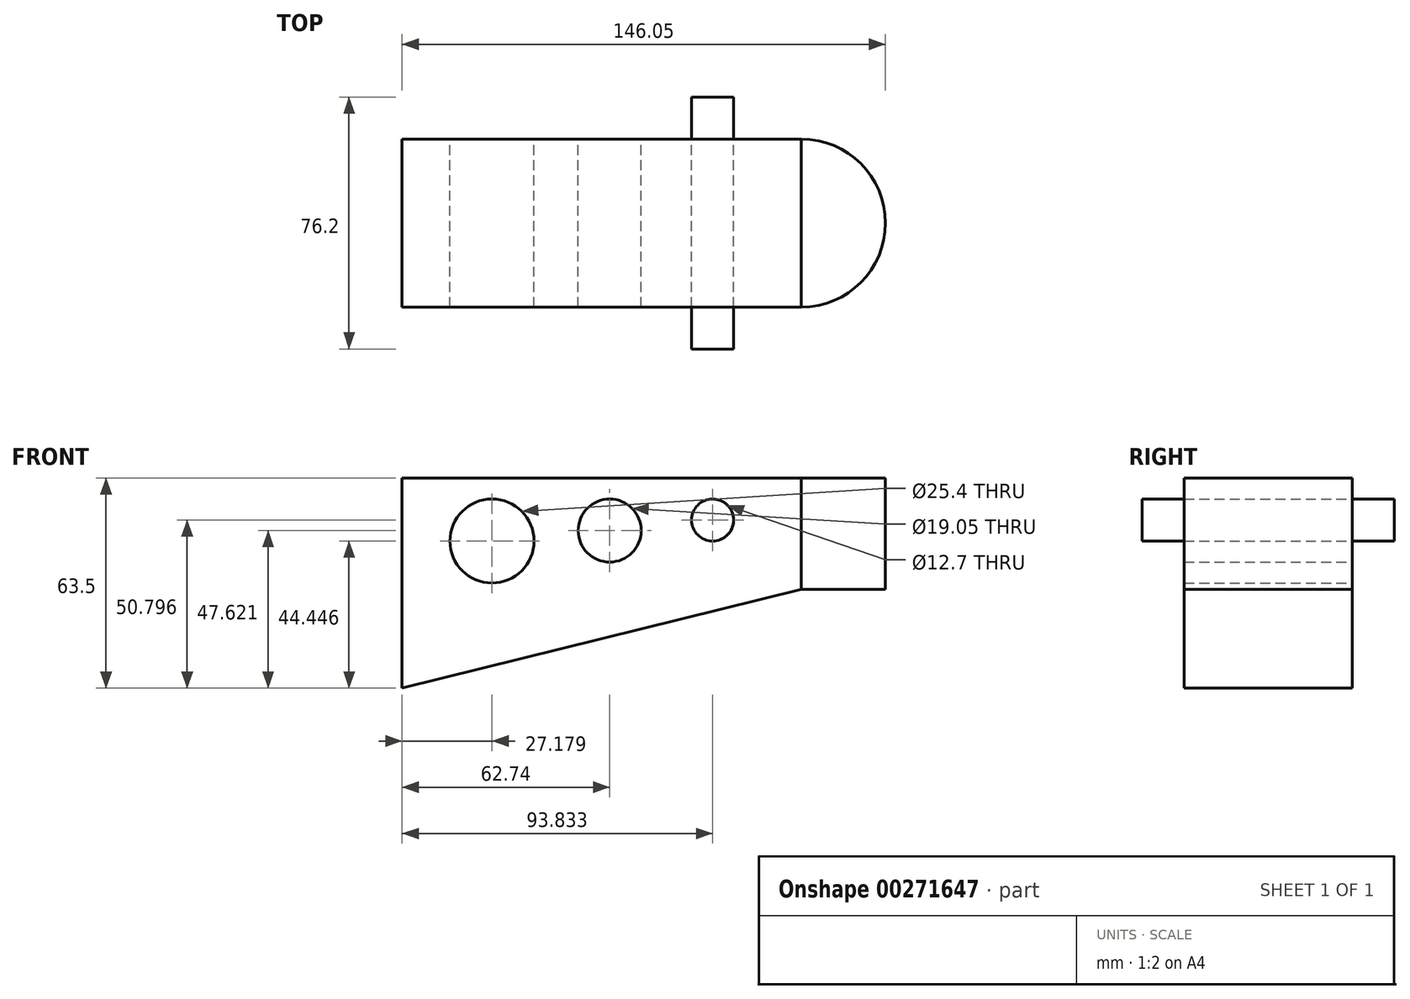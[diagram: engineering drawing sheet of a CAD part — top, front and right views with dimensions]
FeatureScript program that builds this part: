
annotation { "Feature Type Name" : "Feature", "Feature Type Description" : "" }
export const myFeature = defineFeature(function(context is Context, id is Id, definition is map)
    precondition{}
    {
        {
            var Q0;
            Q0=qCreatedBy(makeId("Front.planeOp"),FACE);
            var sketch = newSketch(context, id + "F0", { "sketchPlane" : qUnion([Q0])});
            skLineSegment(sketch, "E0", {"start": v(-62.74, 45.63) * mm, "end": v(-62.74, -17.87) * mm});
            skLineSegment(sketch, "E1", {"start": v(-62.74, -17.87) * mm, "end": v(57.9, 11.92) * mm});
            skLineSegment(sketch, "E2", {"start": v(57.9, 11.92) * mm, "end": v(57.9, 45.63) * mm});
            skLineSegment(sketch, "E3", {"start": v(57.9, 45.63) * mm, "end": v(-62.74, 45.63) * mm});
            skLineSegment(sketch, "E4.bottom", {"start": v(57.9, 45.63) * mm, "end": v(83.3, 45.63) * mm});
            skLineSegment(sketch, "E4.top", {"start": v(57.9, 11.92) * mm, "end": v(83.3, 11.92) * mm});
            skLineSegment(sketch, "E4.left", {"start": v(57.9, 45.63) * mm, "end": v(57.9, 11.92) * mm});
            skLineSegment(sketch, "E4.right", {"start": v(83.3, 45.63) * mm, "end": v(83.3, 11.92) * mm});
            skCircle(sketch, "E5", {"center": v(-35.56, 26.58) * mm, "radius": 12.7 * mm});
            skCircle(sketch, "E6", {"center": v(0, 29.75) * mm, "radius": 9.53 * mm});
            skCircle(sketch, "E7", {"center": v(31.1, 32.93) * mm, "radius": 6.35 * mm});
            skSolve(sketch);
        }
        {
            var Q0;
            Q0=makeQuery(id+"F0.imprint","IMPRINT",FACE,{"disambiguationData":[TD([[makeQuery(id+"F0.imprint","IMPRINT",EDGE,{"derivedFrom":sQuery(id+"F0.wireOp",EDGE,"E0")}),1.0]])]});
            extrude(context, id + "F1", {"entities" : qUnion([Q0]), "endBound" : BoundingType.SYMMETRIC, "depth" : 50.8 * mm});
        }
        {
            var Q0;
            Q0=qCreatedBy(makeId("Front.planeOp"),FACE);
            var sketch = newSketch(context, id + "F2", { "sketchPlane" : qUnion([Q0])});
            skCircle(sketch, "E8", {"center": v(31.1, 32.93) * mm, "radius": 6.35 * mm});
            skSolve(sketch);
        }
        {
            var Q0;
            Q0=makeQuery(id+"F2.imprint","IMPRINT",FACE,{"disambiguationData":[TD([[makeQuery(id+"F2.imprint","IMPRINT",EDGE,{"derivedFrom":sQuery(id+"F2.wireOp",EDGE,"E8")}),1.0]])]});
            extrude(context, id + "F3", {"entities" : qUnion([Q0]), "endBound" : BoundingType.SYMMETRIC, "depth" : 76.2 * mm});
        }
        {
            var Q0;
            Q0=makeQuery(id+"F0.imprint","IMPRINT",FACE,{"disambiguationData":[TD([[makeQuery(id+"F0.imprint","IMPRINT",EDGE,{"derivedFrom":sQuery(id+"F0.wireOp",EDGE,"E4.bottom")}),-1.0]])]});
            var Q1;
            Q1=sQuery(id+"F0.wireOp",EDGE,"E4.left");
            revolve(context, id + "F4", {"entities" : qUnion([Q0]), "axis" : qUnion([Q1]), "revolveType" : RevolveType.SYMMETRIC, "angle" : 180 * degree});
        }
    });
